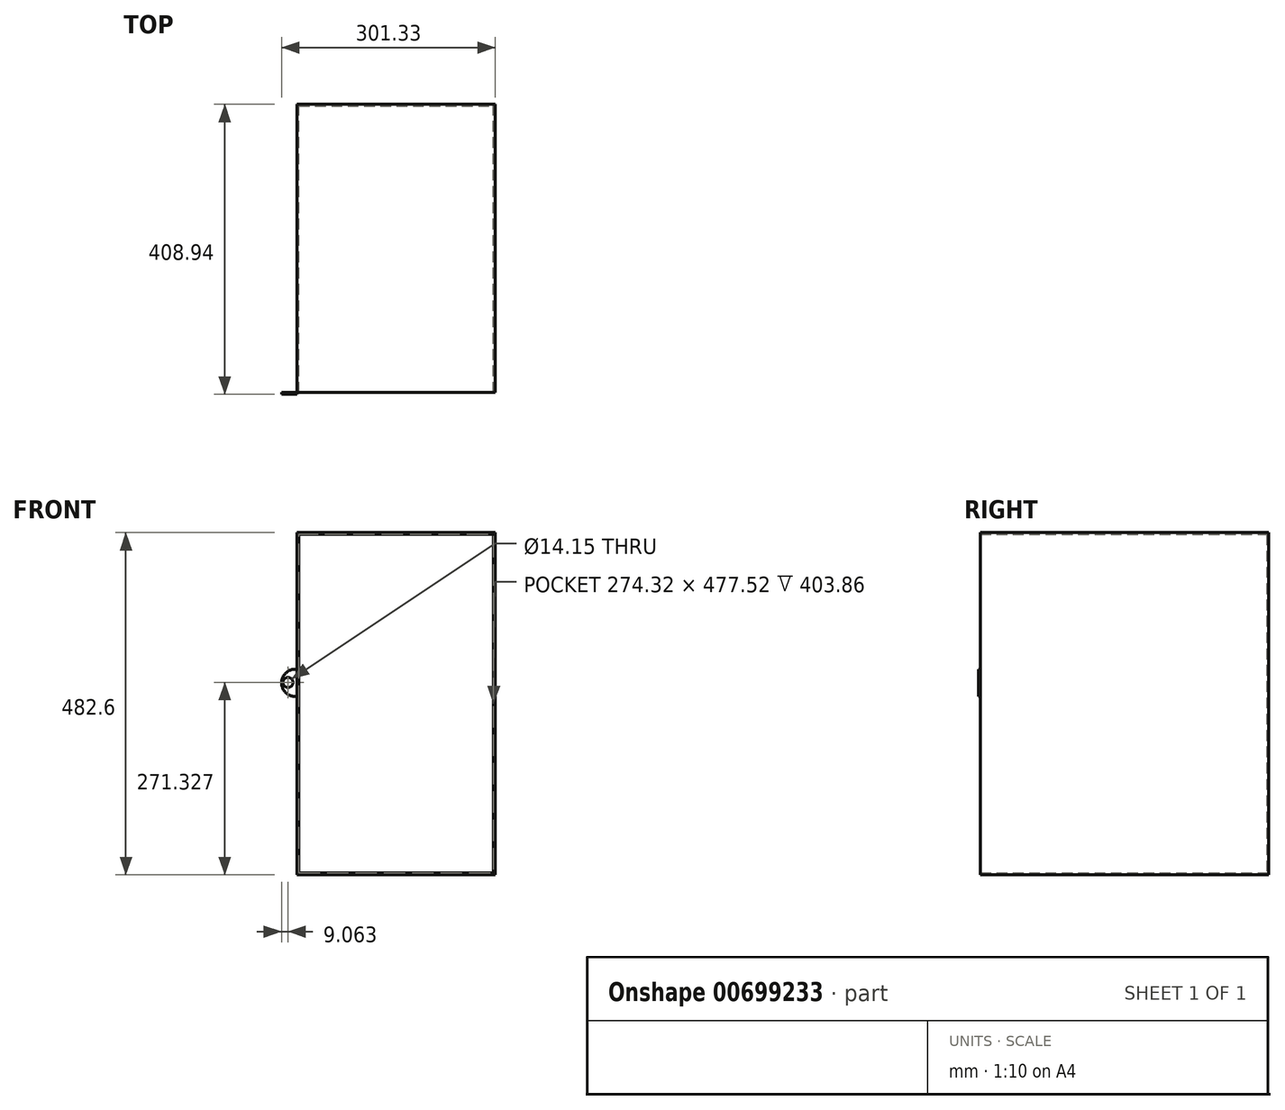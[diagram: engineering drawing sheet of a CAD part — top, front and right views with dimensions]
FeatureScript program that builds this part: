
annotation { "Feature Type Name" : "Feature", "Feature Type Description" : "" }
export const myFeature = defineFeature(function(context is Context, id is Id, definition is map)
    precondition{}
    {
        {
            var Q0;
            Q0=qCreatedBy(makeId("Front.planeOp"),FACE);
            var sketch = newSketch(context, id + "F0", { "sketchPlane" : qUnion([Q0])});
            skLineSegment(sketch, "E0.bottom", {"start": v(-139.7, 241.3) * mm, "end": v(139.7, 241.3) * mm});
            skLineSegment(sketch, "E0.top", {"start": v(-139.7, -241.3) * mm, "end": v(139.7, -241.3) * mm});
            skLineSegment(sketch, "E0.left", {"start": v(-139.7, 241.3) * mm, "end": v(-139.7, -241.3) * mm});
            skLineSegment(sketch, "E0.right", {"start": v(139.7, 241.3) * mm, "end": v(139.7, -241.3) * mm});
            skPoint(sketch, "E0.middle", {"position": v(0, 0) * mm});
            skSolve(sketch);
        }
        {
            var Q0;
            Q0=makeQuery(id+"F0.imprint","IMPRINT",FACE,{"disambiguationData":[TD([[makeQuery(id+"F0.imprint","IMPRINT",EDGE,{"derivedFrom":sQuery(id+"F0.wireOp",EDGE,"E0.bottom")}),-1.0]])]});
            extrude(context, id + "F1", {"entities" : qUnion([Q0]), "depth" : 25.4 * mm, "offsetDistance" : 25.4 * mm});
        }
        {
            var Q0;
            Q0=makeQuery(id+"F1.opExtrude","CAP_FACE",FACE,{"disambiguationData":[OSD([sQuery(id+"F0.wireOp",EDGE,"E0.bottom"),sQuery(id+"F0.wireOp",EDGE,"E0.top"),sQuery(id+"F0.wireOp",EDGE,"E0.left"),sQuery(id+"F0.wireOp",EDGE,"E0.right")])],"isStart":false});
            extrude(context, id + "F2", {"entities" : qUnion([Q0]), "operationType" : NewBodyOperationType.ADD, "depth" : 381 * mm, "offsetDistance" : 25.4 * mm});
        }
        {
            var Q0;
            Q0=makeQuery(id+"F2.opExtrude","CAP_FACE",FACE,{"disambiguationData":[OSD([sQuery(id+"F0.wireOp",EDGE,"E0.bottom"),sQuery(id+"F0.wireOp",EDGE,"E0.top"),sQuery(id+"F0.wireOp",EDGE,"E0.left"),sQuery(id+"F0.wireOp",EDGE,"E0.right")])],"isStart":false});
            shell(context, id + "F3", {"entities" : qUnion([Q0]), "thickness" : 2.54 * mm});
        }
        {
            var Q0;
            Q0=makeQuery(id+"F2.opExtrude","CAP_FACE",FACE,{"disambiguationData":[OSD([sQuery(id+"F0.wireOp",EDGE,"E0.bottom"),sQuery(id+"F0.wireOp",EDGE,"E0.top"),sQuery(id+"F0.wireOp",EDGE,"E0.left"),sQuery(id+"F0.wireOp",EDGE,"E0.right")])],"isStart":false});
            var sketch = newSketch(context, id + "F4", { "sketchPlane" : qUnion([Q0])});
            skArc(sketch, "E1", {"start": v(-139.7, 48.48) * mm, "mid": v(-161.63, 29.47) * mm, "end": v(-139.7, 10.46) * mm});
            skPoint(sketch, "E2", {"position": v(-152.49, 29.47) * mm});
            skCircle(sketch, "E3", {"center": v(-152.57, 30.03) * mm, "radius": 7.07 * mm});
            skSolve(sketch);
        }
        {
            var Q0;
            {var subQ0=sQuery(id+"F4.wireOp",EDGE,"E1");Q0=makeQuery(id+"F4.imprint","IMPRINT",FACE,{"disambiguationData":[TD([[makeQuery(id+"F4.imprint","IMPRINT",EDGE,{"derivedFrom":subQ0}),1.0]])]});}
            extrude(context, id + "F5", {"entities" : qUnion([Q0]), "depth" : 2.54 * mm, "offsetDistance" : 25.4 * mm});
        }
    });
